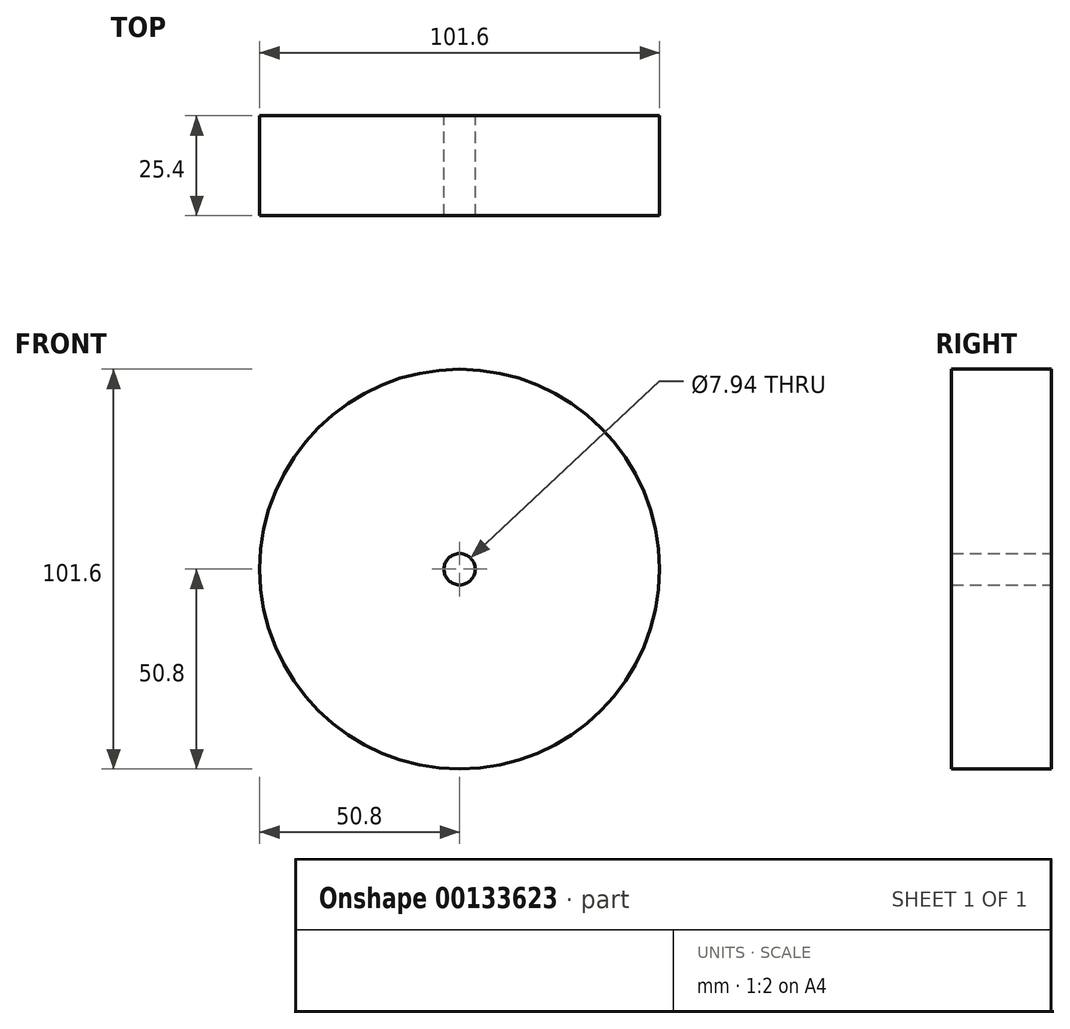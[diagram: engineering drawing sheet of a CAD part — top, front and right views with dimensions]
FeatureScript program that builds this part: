
annotation { "Feature Type Name" : "Feature", "Feature Type Description" : "" }
export const myFeature = defineFeature(function(context is Context, id is Id, definition is map)
    precondition{}
    {
        {
            var Q0;
            Q0=qCreatedBy(makeId("Front.planeOp"),FACE);
            var sketch = newSketch(context, id + "F0", { "sketchPlane" : qUnion([Q0])});
            skCircle(sketch, "E0", {"center": v(0, 0) * mm, "radius": 50.8 * mm});
            skCircle(sketch, "E1", {"center": v(548.54, -881.35) * mm, "radius": 385.91 * mm});
            skCircle(sketch, "E2", {"center": v(0, 0) * mm, "radius": 3.97 * mm});
            skSolve(sketch);
        }
        {
            var Q0;
            Q0=makeQuery(id+"F0.imprint","IMPRINT",FACE,{"disambiguationData":[TD([[makeQuery(id+"F0.imprint","IMPRINT",EDGE,{"derivedFrom":sQuery(id+"F0.wireOp",EDGE,"E0")}),1.0]])]});
            extrude(context, id + "F1", {"entities" : qUnion([Q0]), "depth" : 25.4 * mm, "offsetDistance" : 25.4 * mm});
        }
    });
